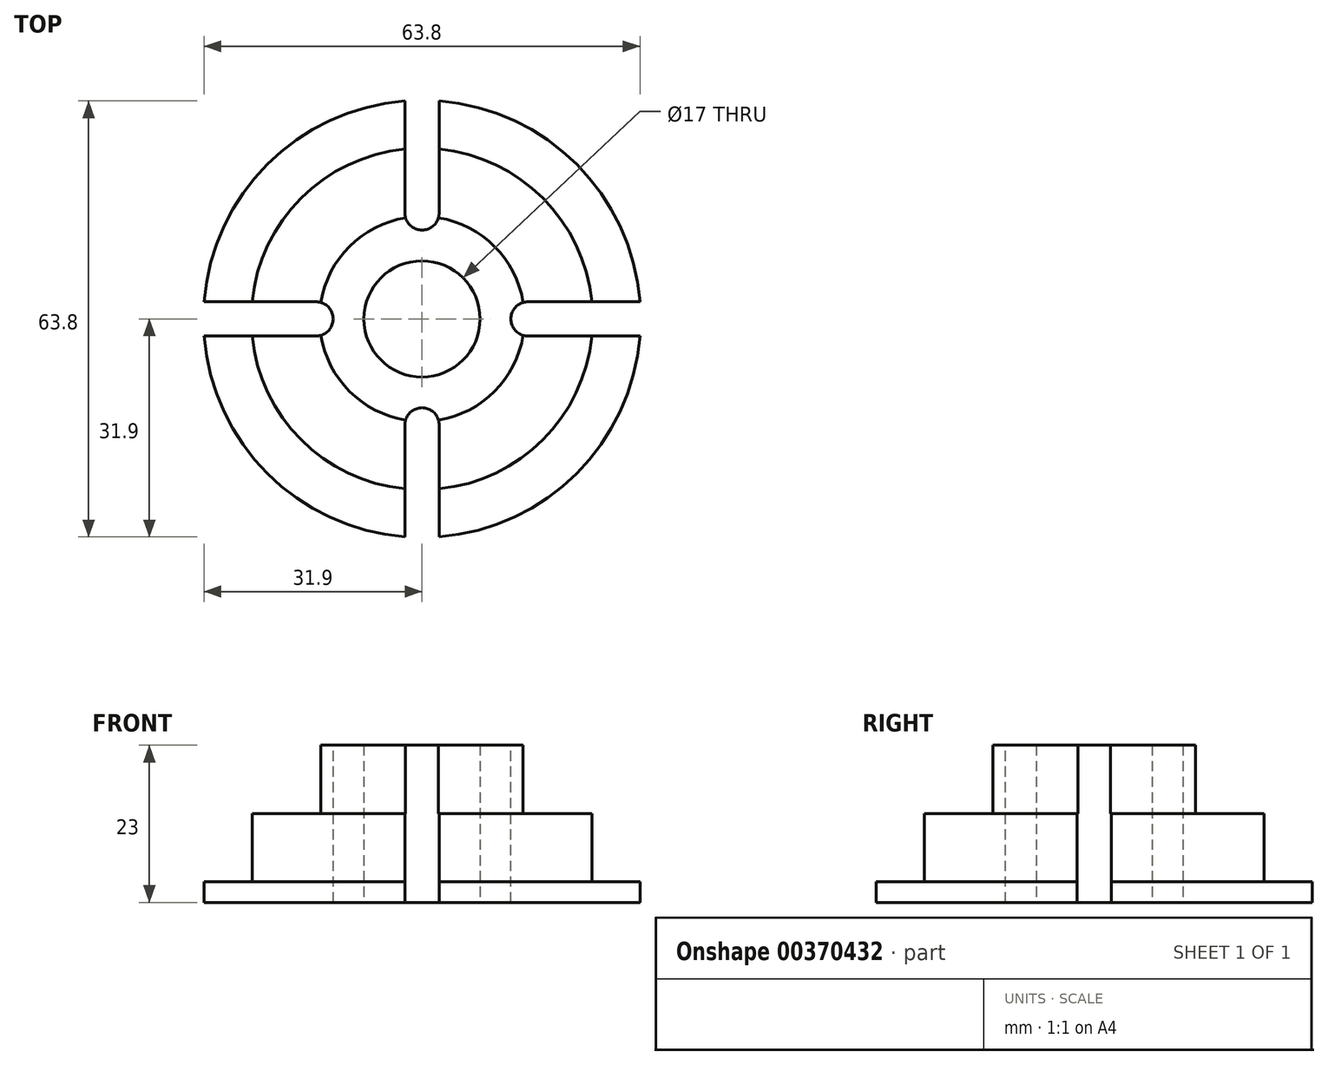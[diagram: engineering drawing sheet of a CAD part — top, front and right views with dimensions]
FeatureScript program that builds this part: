
annotation { "Feature Type Name" : "Feature", "Feature Type Description" : "" }
export const myFeature = defineFeature(function(context is Context, id is Id, definition is map)
    precondition{}
    {
        {
            var Q0;
            Q0=qCreatedBy(makeId("Right.planeOp"),FACE);
            var sketch = newSketch(context, id + "F0", { "sketchPlane" : qUnion([Q0])});
            skLineSegment(sketch, "E0", {"start": v(8.5, 0) * mm, "end": v(8.5, 23) * mm});
            skLineSegment(sketch, "E1", {"start": v(8.5, 23) * mm, "end": v(15, 23) * mm});
            skLineSegment(sketch, "E2", {"start": v(32, 0) * mm, "end": v(8.5, 0) * mm});
            skLineSegment(sketch, "E3", {"start": v(0, 0) * mm, "end": v(0, 63.53) * mm});
            skLineSegment(sketch, "E4", {"start": v(25, 13) * mm, "end": v(25, 3) * mm});
            skLineSegment(sketch, "E5", {"start": v(25, 3) * mm, "end": v(32, 3) * mm});
            skLineSegment(sketch, "E6", {"start": v(32, 3) * mm, "end": v(32, 0) * mm});
            skLineSegment(sketch, "E7", {"start": v(15, 23) * mm, "end": v(15, 13) * mm});
            skLineSegment(sketch, "E8", {"start": v(15, 13) * mm, "end": v(25, 13) * mm});
            skSolve(sketch);
        }
        {
            var Q0;
            Q0=makeQuery(id+"F0.imprint","IMPRINT",FACE,{"disambiguationData":[TD([[makeQuery(id+"F0.imprint","IMPRINT",EDGE,{"derivedFrom":sQuery(id+"F0.wireOp",EDGE,"E0")}),-1.0]])]});
            var Q1;
            Q1=sQuery(id+"F0.wireOp",EDGE,"E3");
            revolve(context, id + "F1", {"entities" : qUnion([Q0]), "axis" : qUnion([Q1]), "revolveType" : RevolveType.FULL});
        }
        {
            var Q0;
            Q0=makeQuery(id+"F1.opRevolve","SWEPT_FACE",FACE,{"disambiguationData":[OSD([sQuery(id+"F0.wireOp",EDGE,"E2")])]});
            var sketch = newSketch(context, id + "F2", { "sketchPlane" : qUnion([Q0])});
            skLineSegment(sketch, "E9.bottom", {"start": v(2.5, 13) * mm, "end": v(-2.5, 13) * mm});
            skLineSegment(sketch, "E9.top", {"start": v(2.5, 43) * mm, "end": v(-2.5, 43) * mm});
            skLineSegment(sketch, "E9.left", {"start": v(2.5, 13) * mm, "end": v(2.5, 43) * mm});
            skLineSegment(sketch, "E9.right", {"start": v(-2.5, 13) * mm, "end": v(-2.5, 43) * mm});
            skPoint(sketch, "E9.middle", {"position": v(0, 28) * mm});
            skLineSegment(sketch, "E10.1.0", {"start": v(-13, 2.5) * mm, "end": v(-13, -2.5) * mm});
            skLineSegment(sketch, "E10.1.1", {"start": v(-13, -2.5) * mm, "end": v(-43, -2.5) * mm});
            skLineSegment(sketch, "E10.1.2", {"start": v(-13, 2.5) * mm, "end": v(-43, 2.5) * mm});
            skLineSegment(sketch, "E10.1.3", {"start": v(-43, 2.5) * mm, "end": v(-43, -2.5) * mm});
            skLineSegment(sketch, "E10.2.0", {"start": v(-2.5, -13) * mm, "end": v(2.5, -13) * mm});
            skLineSegment(sketch, "E10.2.1", {"start": v(2.5, -13) * mm, "end": v(2.5, -43) * mm});
            skLineSegment(sketch, "E10.2.2", {"start": v(-2.5, -13) * mm, "end": v(-2.5, -43) * mm});
            skLineSegment(sketch, "E10.2.3", {"start": v(-2.5, -43) * mm, "end": v(2.5, -43) * mm});
            skLineSegment(sketch, "E10.3.0", {"start": v(13, -2.5) * mm, "end": v(13, 2.5) * mm});
            skLineSegment(sketch, "E10.3.1", {"start": v(13, 2.5) * mm, "end": v(43, 2.5) * mm});
            skLineSegment(sketch, "E10.3.2", {"start": v(13, -2.5) * mm, "end": v(43, -2.5) * mm});
            skLineSegment(sketch, "E10.3.3", {"start": v(43, -2.5) * mm, "end": v(43, 2.5) * mm});
            skPoint(sketch, "E10.center", {"position": v(0, 0) * mm});
            skSolve(sketch);
        }
        {
            var Q0;
            {var subQ0=sQuery(id+"F2.wireOp",EDGE,"E9.bottom");Q0=makeQuery(id+"F2.imprint","IMPRINT",FACE,{"disambiguationData":[TD([[makeQuery(id+"F2.imprint","IMPRINT",EDGE,{"derivedFrom":subQ0}),-1.0]])]});}
            var Q1;
            {var subQ0=sQuery(id+"F2.wireOp",EDGE,"E10.3.0");Q1=makeQuery(id+"F2.imprint","IMPRINT",FACE,{"disambiguationData":[TD([[makeQuery(id+"F2.imprint","IMPRINT",EDGE,{"derivedFrom":subQ0}),-1.0]])]});}
            var Q2;
            {var subQ0=sQuery(id+"F2.wireOp",EDGE,"E10.2.0");Q2=makeQuery(id+"F2.imprint","IMPRINT",FACE,{"disambiguationData":[TD([[makeQuery(id+"F2.imprint","IMPRINT",EDGE,{"derivedFrom":subQ0}),-1.0]])]});}
            var Q3;
            {var subQ0=sQuery(id+"F2.wireOp",EDGE,"E10.1.0");Q3=makeQuery(id+"F2.imprint","IMPRINT",FACE,{"disambiguationData":[TD([[makeQuery(id+"F2.imprint","IMPRINT",EDGE,{"derivedFrom":subQ0}),-1.0]])]});}
            extrude(context, id + "F3", {"entities" : qUnion([Q0, Q1, Q2, Q3]), "operationType" : NewBodyOperationType.REMOVE, "endBound" : BoundingType.UP_TO_NEXT, "oppositeDirection" : true, "depth" : 25 * mm});
        }
        {
            var Q0;
            Q0=makeQuery(id+"F3.boolean.opBoolean","COPY",EDGE,{"derivedFrom":makeQuery(id+"F3.opExtrude","SWEPT_EDGE",EDGE,{"disambiguationData":[OSD([sQuery(id+"F2.wireOp",EDGE,"E9.bottom"),sQuery(id+"F2.wireOp",EDGE,"E9.right")])]})});
            var Q1;
            Q1=makeQuery(id+"F3.boolean.opBoolean","COPY",EDGE,{"derivedFrom":makeQuery(id+"F3.opExtrude","SWEPT_EDGE",EDGE,{"disambiguationData":[OSD([sQuery(id+"F2.wireOp",EDGE,"E9.bottom"),sQuery(id+"F2.wireOp",EDGE,"E9.left")])]})});
            var Q2;
            Q2=makeQuery(id+"F3.boolean.opBoolean","COPY",EDGE,{"derivedFrom":makeQuery(id+"F3.opExtrude","SWEPT_EDGE",EDGE,{"disambiguationData":[OSD([sQuery(id+"F2.wireOp",EDGE,"E10.3.0"),sQuery(id+"F2.wireOp",EDGE,"E10.3.1")])]})});
            var Q3;
            Q3=makeQuery(id+"F3.boolean.opBoolean","COPY",EDGE,{"derivedFrom":makeQuery(id+"F3.opExtrude","SWEPT_EDGE",EDGE,{"disambiguationData":[OSD([sQuery(id+"F2.wireOp",EDGE,"E10.3.0"),sQuery(id+"F2.wireOp",EDGE,"E10.3.2")])]})});
            var Q4;
            Q4=makeQuery(id+"F3.boolean.opBoolean","COPY",EDGE,{"derivedFrom":makeQuery(id+"F3.opExtrude","SWEPT_EDGE",EDGE,{"disambiguationData":[OSD([sQuery(id+"F2.wireOp",EDGE,"E10.2.0"),sQuery(id+"F2.wireOp",EDGE,"E10.2.2")])]})});
            var Q5;
            Q5=makeQuery(id+"F3.boolean.opBoolean","COPY",EDGE,{"derivedFrom":makeQuery(id+"F3.opExtrude","SWEPT_EDGE",EDGE,{"disambiguationData":[OSD([sQuery(id+"F2.wireOp",EDGE,"E10.2.0"),sQuery(id+"F2.wireOp",EDGE,"E10.2.1")])]})});
            var Q6;
            Q6=makeQuery(id+"F3.boolean.opBoolean","COPY",EDGE,{"derivedFrom":makeQuery(id+"F3.opExtrude","SWEPT_EDGE",EDGE,{"disambiguationData":[OSD([sQuery(id+"F2.wireOp",EDGE,"E10.1.0"),sQuery(id+"F2.wireOp",EDGE,"E10.1.1")])]})});
            var Q7;
            Q7=makeQuery(id+"F3.boolean.opBoolean","COPY",EDGE,{"derivedFrom":makeQuery(id+"F3.opExtrude","SWEPT_EDGE",EDGE,{"disambiguationData":[OSD([sQuery(id+"F2.wireOp",EDGE,"E10.1.0"),sQuery(id+"F2.wireOp",EDGE,"E10.1.2")])]})});
            fillet(context, id + "F4", {"entities" : qUnion([Q0, Q1, Q2, Q3, Q4, Q5, Q6, Q7]), "radius" : 2.5 * mm, "tangentPropagation" : true, "allowEdgeOverflow" : false});
        }
    });
